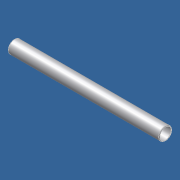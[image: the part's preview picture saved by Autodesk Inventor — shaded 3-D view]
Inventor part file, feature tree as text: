
AUTODESK INVENTOR PART (.ipt)
format: ipt  version: 2012 (Build 160160000, 160)  size: 105,984 bytes
history: native  units: in
note: dims shown in document units (in); Inventor stores cm internally (conversion verified against a paired STEP export)
features: other x42, revolve x1, sketch x1
ambient origin geometry x8: Origin, YZ Plane, XZ Plane, XY Plane, X Axis, Y Axis, Z Axis, Center Point
bodies: Solid1 (feature_tree)
feature tree (44):
  revolve  "Revolution1"  [1 undecoded]
  other  "tube_front_XY"
  other  "tube_front_YZ"
  other  "tube_front_ZX"
  other  "tube_front_X"
  other  "tube_front_Y"
  other  "tube_front_Z"
  other  "tube_front_Center"
  other  "tube_rear_XY"
  other  "tube_rear_YZ"
  other  "tube_rear_ZX"
  other  "tube_rear_X"
  other  "tube_rear_Y"
  other  "tube_rear_Z"
  other  "tube_rear_Center"
  other  "cp1_XY"
  other  "cp1_YZ"
  other  "cp1_ZX"
  other  "cp1_X"
  other  "cp1_Y"
  other  "cp1_Z"
  other  "cp1_Center"
  other  "cp2_XY"
  other  "cp2_YZ"
  other  "cp2_ZX"
  other  "cp2_X"
  other  "cp2_Y"
  other  "cp2_Z"
  other  "cp2_Center"
  other  "cp3_XY"
  other  "cp3_YZ"
  other  "cp3_ZX"
  other  "cp3_X"
  other  "cp3_Y"
  other  "cp3_Z"
  other  "cp3_Center"
  other  "cp4_XY"
  other  "cp4_YZ"
  other  "cp4_ZX"
  other  "cp4_X"
  other  "cp4_Y"
  other  "cp4_Z"
  other  "cp4_Center"
  sketch  "Sketch_1"  dims[d0=360.0deg]
note: 1 required parameter value undecoded (feature->parameter linkage not recoverable at this tier; creation-order binding heuristic only, values carry confidence <= 0.55)
